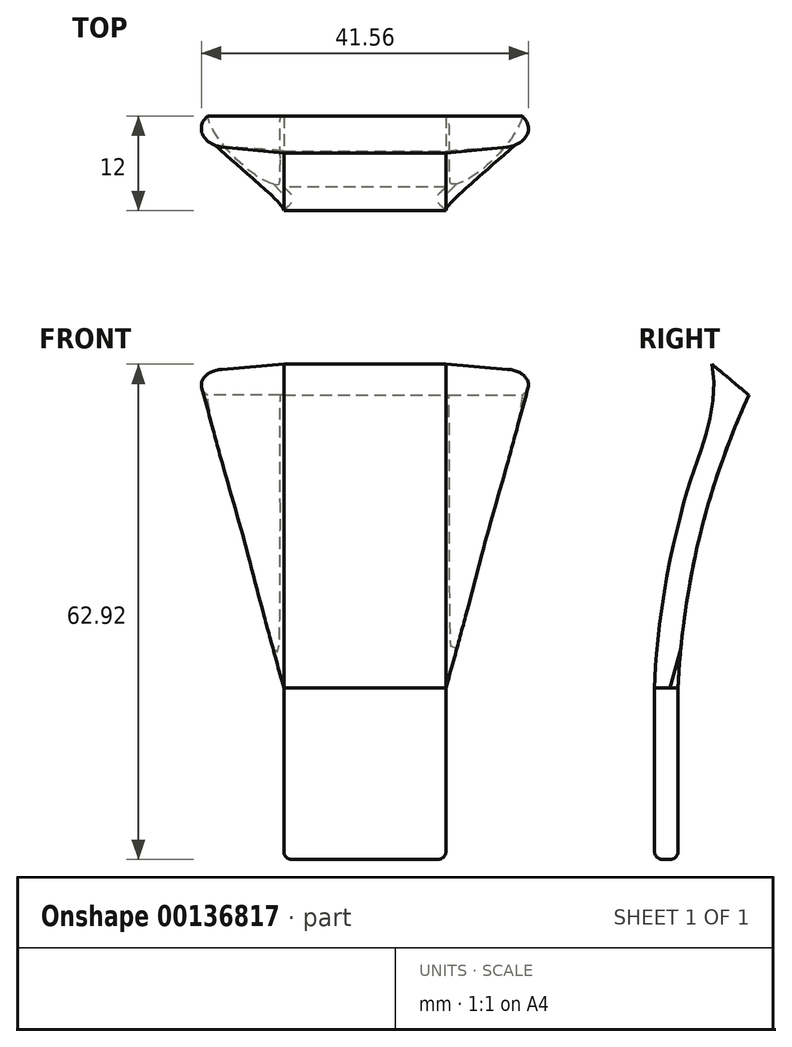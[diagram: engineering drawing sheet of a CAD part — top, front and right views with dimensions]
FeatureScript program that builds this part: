
annotation { "Feature Type Name" : "Feature", "Feature Type Description" : "" }
export const myFeature = defineFeature(function(context is Context, id is Id, definition is map)
    precondition{}
    {
        {
            var Q0;
            Q0=qCreatedBy(makeId("Front.planeOp"),FACE);
            var sketch = newSketch(context, id + "F0", { "sketchPlane" : qUnion([Q0])});
            skLineSegment(sketch, "E0.bottom", {"start": v(0, 0) * mm, "end": v(-20.6, 0) * mm});
            skLineSegment(sketch, "E0.top", {"start": v(0, 21.8) * mm, "end": v(-20.6, 21.8) * mm});
            skLineSegment(sketch, "E0.left", {"start": v(0, 0) * mm, "end": v(0, 21.8) * mm});
            skLineSegment(sketch, "E0.right", {"start": v(-20.6, 0) * mm, "end": v(-20.6, 21.8) * mm});
            skLineSegment(sketch, "E1", {"start": v(-10.3, 21.8) * mm, "end": v(-10.3, 0) * mm, "construction": true});
            skSolve(sketch);
        }
        {
            var Q0;
            Q0 = qSketchRegion(id + "F0", true);
            var Q1;
            Q1=makeQuery(id+"F0.imprint","IMPRINT",FACE,{"disambiguationData":[TD([[makeQuery(id+"F0.imprint","IMPRINT",EDGE,{"derivedFrom":sQuery(id+"F0.wireOp",EDGE,"E0.bottom")}),-1.0]])]});
            extrude(context, id + "F1", {"entities" : qUnion([Q0, Q1]), "depth" : 3 * mm});
        }
        {
            var Q0;
            Q0=qCreatedBy(makeId("Right.planeOp"),FACE);
            var sketch = newSketch(context, id + "F2", { "sketchPlane" : qUnion([Q0])});
            skArc(sketch, "E2", {"start": v(9, 58.98) * mm, "mid": v(2.7, 40.83) * mm, "end": v(0, 21.8) * mm});
            skLineSegment(sketch, "E3", {"start": v(9, 58.98) * mm, "end": v(9, 21.8) * mm, "construction": true});
            skLineSegment(sketch, "E4", {"start": v(0, 21.8) * mm, "end": v(-3, 21.8) * mm});
            skLineSegment(sketch, "E5", {"start": v(0, 21.8) * mm, "end": v(9, 21.8) * mm, "construction": true});
            skLineSegment(sketch, "E6", {"start": v(9, 58.98) * mm, "end": v(6.6, 61) * mm});
            skLineSegment(sketch, "E7", {"start": v(9, 58.98) * mm, "end": v(-3.17, 58.98) * mm, "construction": true});
            skLineSegment(sketch, "E8", {"start": v(6.6, 61) * mm, "end": v(4.3, 62.92) * mm});
            skFitSpline(sketch, "E9", {"points": [v(-3, 21.8) * mm, v(-2.7, 26.37) * mm, v(-1.58, 35) * mm, v(0.14, 43) * mm, v(1.64, 48.28) * mm, v(3.1, 52.6) * mm, v(4.3, 62.92) * mm], "startDerivative": vector(1.53, 30.61) * mm, "endDerivative": vector(-11.43, 51.05) * mm});
            skSolve(sketch);
        }
        {
            var Q0;
            Q0 = qSketchRegion(id + "F2", true);
            var Q1;
            Q1=makeQuery(id+"F2.imprint","IMPRINT",FACE,{"disambiguationData":[TD([[makeQuery(id+"F2.imprint","IMPRINT",EDGE,{"derivedFrom":sQuery(id+"F2.wireOp",EDGE,"E2")}),-1.0]])]});
            extrude(context, id + "F3", {"entities" : qUnion([Q0, Q1]), "oppositeDirection" : true, "depth" : 20.6 * mm});
        }
        {
            var Q0;
            Q0=makeQuery(id+"F1.opExtrude","SWEPT_EDGE",EDGE,{"disambiguationData":[OSD([sQuery(id+"F0.wireOp",EDGE,"E0.bottom"),sQuery(id+"F0.wireOp",EDGE,"E0.left")])]});
            var Q1;
            Q1=makeQuery(id+"F1.opExtrude","CAP_EDGE",EDGE,{"disambiguationData":[OSD([sQuery(id+"F0.wireOp",EDGE,"E0.bottom")])],"isStart":false});
            var Q2;
            Q2=makeQuery(id+"F1.opExtrude","SWEPT_EDGE",EDGE,{"disambiguationData":[OSD([sQuery(id+"F0.wireOp",EDGE,"E0.bottom"),sQuery(id+"F0.wireOp",EDGE,"E0.right")])]});
            var Q3;
            Q3=makeQuery(id+"F1.opExtrude","CAP_EDGE",EDGE,{"disambiguationData":[OSD([sQuery(id+"F0.wireOp",EDGE,"E0.bottom")])],"isStart":true});
            fillet(context, id + "F4", {"entities" : qUnion([Q0, Q1, Q2, Q3]), "radius" : 1 * mm, "tangentPropagation" : true, "allowEdgeOverflow" : false});
        }
        {
            var Q0;
            Q0=makeQuery(id+"F3.opExtrude","SWEPT_FACE",FACE,{"disambiguationData":[OSD([sQuery(id+"F2.wireOp",EDGE,"E6"),sQuery(id+"F2.wireOp",EDGE,"E8")])]});
            var sketch = newSketch(context, id + "F5", { "sketchPlane" : qUnion([Q0])});
            skLineSegment(sketch, "E10", {"start": v(0, -31.02) * mm, "end": v(9.69, -31.02) * mm});
            skLineSegment(sketch, "E11", {"start": v(7.82, -36.12) * mm, "end": v(0, -37.16) * mm});
            skArc(sketch, "E12", {"start": v(7.82, -36.12) * mm, "mid": v(10.3, -34.13) * mm, "end": v(9.69, -31.02) * mm});
            skLineSegment(sketch, "E13", {"start": v(-10.3, -31.02) * mm, "end": v(-10.3, -37.16) * mm, "construction": true});
            skLineSegment(sketch, "E14.MirrorCS", {"start": v(-20.6, -31.02) * mm, "end": v(-30.29, -31.02) * mm});
            skLineSegment(sketch, "E15.MirrorCS", {"start": v(-28.42, -36.12) * mm, "end": v(-20.6, -37.16) * mm});
            skArc(sketch, "E16.MirrorCS", {"start": v(-28.42, -36.12) * mm, "mid": v(-30.9, -34.13) * mm, "end": v(-30.29, -31.02) * mm});
            skSolve(sketch);
        }
        {
            var Q0;
            Q0=makeQuery(id+"F1.opExtrude","SWEPT_FACE",FACE,{"disambiguationData":[OSD([sQuery(id+"F0.wireOp",EDGE,"E0.top")])]});
            var sketch = newSketch(context, id + "F6", { "sketchPlane" : qUnion([Q0])});
            skLineSegment(sketch, "E17.bottom", {"start": v(0, 0) * mm, "end": v(-0.5, 0) * mm});
            skLineSegment(sketch, "E17.top", {"start": v(0, -3) * mm, "end": v(-0.5, -3) * mm});
            skLineSegment(sketch, "E17.left", {"start": v(0, 0) * mm, "end": v(0, -3) * mm});
            skLineSegment(sketch, "E17.right", {"start": v(-0.5, 0) * mm, "end": v(-0.5, -3) * mm});
            skLineSegment(sketch, "E18.bottom", {"start": v(-20.6, 0) * mm, "end": v(-20.1, 0) * mm});
            skLineSegment(sketch, "E18.top", {"start": v(-20.6, -3) * mm, "end": v(-20.1, -3) * mm});
            skLineSegment(sketch, "E18.left", {"start": v(-20.6, 0) * mm, "end": v(-20.6, -3) * mm});
            skLineSegment(sketch, "E18.right", {"start": v(-20.1, 0) * mm, "end": v(-20.1, -3) * mm});
            skSolve(sketch);
        }
        {
            var Q0;
            Q0=makeQuery(id+"F5.imprint","IMPRINT",FACE,{"disambiguationData":[TD([[makeQuery(id+"F5.imprint","IMPRINT",EDGE,{"derivedFrom":sQuery(id+"F5.wireOp",EDGE,"E10")}),-1.0]])]});
            var Q1;
            Q1=makeQuery(id+"F6.imprint","IMPRINT",FACE,{"disambiguationData":[TD([[makeQuery(id+"F6.imprint","IMPRINT",EDGE,{"derivedFrom":sQuery(id+"F6.wireOp",EDGE,"E17.bottom")}),1.0]])]});
            var Q2;
            Q2=sQuery(id+"F2.wireOp",EDGE,"E9");
            var Q3;
            Q3=sQuery(id+"F2.wireOp",EDGE,"E2");
            loft(context, id + "F7", {"addGuides" : true, "sheetProfilesArray" : [{ "sheetProfileEntities" : qUnion([Q0]) }, { "sheetProfileEntities" : qUnion([Q1]) }], "guidesArray" : [{ "guideEntities" : qUnion([Q2]), "guideDerivativeType" : LoftGuideDerivativeType.DEFAULT, "guideDerivativeMagnitude" : 1 }, { "guideEntities" : qUnion([Q3]), "guideDerivativeType" : LoftGuideDerivativeType.DEFAULT, "guideDerivativeMagnitude" : 1 }]});
        }
        {
            var Q1;
            Q1=makeQuery(id+"F5.imprint","IMPRINT",FACE,{"disambiguationData":[TD([[makeQuery(id+"F5.imprint","IMPRINT",EDGE,{"derivedFrom":sQuery(id+"F5.wireOp",EDGE,"E14.MirrorCS")}),1.0]])]});
            var Q2;
            Q2=makeQuery(id+"F6.imprint","IMPRINT",FACE,{"disambiguationData":[TD([[makeQuery(id+"F6.imprint","IMPRINT",EDGE,{"derivedFrom":sQuery(id+"F6.wireOp",EDGE,"E18.bottom")}),1.0]])]});
            var Q3;
            Q3=makeQuery(id+"F3.opExtrude","CAP_EDGE",EDGE,{"disambiguationData":[OSD([sQuery(id+"F2.wireOp",EDGE,"E2")])],"isStart":false});
            var Q4;
            Q4=makeQuery(id+"F3.opExtrude","CAP_EDGE",EDGE,{"disambiguationData":[OSD([sQuery(id+"F2.wireOp",EDGE,"E9")])],"isStart":false});
            var Q5;
            Q5=sQuery(id+"F5.wireOp",VERTEX,"E16.MirrorCS.start");
            var Q6;
            Q6=sQuery(id+"F6.wireOp",VERTEX,"E18.left.end");
            loft(context, id + "F8", {"operationType" : NewBodyOperationType.ADD, "addGuides" : true, "sheetProfilesArray" : [{ "sheetProfileEntities" : qUnion([Q1]) }, { "sheetProfileEntities" : qUnion([Q2]) }], "guidesArray" : [{ "guideEntities" : qUnion([Q3]), "guideDerivativeType" : LoftGuideDerivativeType.DEFAULT, "guideDerivativeMagnitude" : 1 }, { "guideEntities" : qUnion([Q4]), "guideDerivativeType" : LoftGuideDerivativeType.DEFAULT, "guideDerivativeMagnitude" : 1 }], "connections" : [{ "connectionEntities" : qUnion([Q5, Q6]), "connectionEdgeQueries" : qUnion([]), "connectionEdgeParameters" : [] }]});
        }
        {
            var Q0;
            Q0=makeQuery(id+"F0.imprint","IMPRINT",FACE,{"disambiguationData":[TD([[makeQuery(id+"F0.imprint","IMPRINT",EDGE,{"derivedFrom":sQuery(id+"F0.wireOp",EDGE,"E0.bottom")}),-1.0]])]});
            extrude(context, id + "F9", {"entities" : qUnion([Q0]), "depth" : 3 * mm});
        }
        {
            var Q0;
            Q0 = qSketchRegion(id + "F2", true);
            extrude(context, id + "F10", {"entities" : qUnion([Q0]), "operationType" : NewBodyOperationType.INTERSECT, "endBound" : BoundingType.SYMMETRIC, "oppositeDirection" : true, "depth" : 100 * mm, "hasSecondDirection" : true, "secondDirectionOppositeDirection" : false, "secondDirectionDepth" : 25 * mm});
        }
        {
            var Q0;
            Q0 = qSketchRegion(id + "F0", true);
            var Q1;
            Q1=makeQuery(id+"F0.imprint","IMPRINT",FACE,{"disambiguationData":[TD([[makeQuery(id+"F0.imprint","IMPRINT",EDGE,{"derivedFrom":sQuery(id+"F0.wireOp",EDGE,"E0.bottom")}),-1.0]])]});
            extrude(context, id + "F11", {"entities" : qUnion([Q0, Q1]), "operationType" : NewBodyOperationType.ADD, "depth" : 3 * mm});
        }
        {
            var Q0;
            Q0=makeQuery(id+"F11.opExtrude","SWEPT_FACE",FACE,{"disambiguationData":[OSD([sQuery(id+"F0.wireOp",EDGE,"E0.bottom")])]});
            fillet(context, id + "F12", {"entities" : qUnion([Q0]), "radius" : 1 * mm, "tangentPropagation" : true, "allowEdgeOverflow" : false});
        }
        {
            var Q0;
            Q0=makeQuery(id+"F1.opExtrude","SWEPT_BODY",BODY,{"disambiguationData":[OSD([sQuery(id+"F0.wireOp",EDGE,"E0.bottom"),sQuery(id+"F0.wireOp",EDGE,"E0.top"),sQuery(id+"F0.wireOp",EDGE,"E0.left"),sQuery(id+"F0.wireOp",EDGE,"E0.right")])]});
            transform(context, id + "F13", {"entities" : qUnion([Q0]), "transformType" : TransformType.TRANSLATION_3D, "dx" : 0 * mm, "dy" : 0 * mm, "dz" : 0 * mm, "makeCopy" : true});
        }
        {
            var Q0;
            Q0=makeQuery(id+"F13.opPattern","COPY",BODY,{"derivedFrom":makeQuery(id+"F1.opExtrude","SWEPT_BODY",BODY,{"disambiguationData":[OSD([sQuery(id+"F0.wireOp",EDGE,"E0.bottom"),sQuery(id+"F0.wireOp",EDGE,"E0.top"),sQuery(id+"F0.wireOp",EDGE,"E0.left"),sQuery(id+"F0.wireOp",EDGE,"E0.right")])]}),"instanceName":"1"});
            deleteBodies(context, id + "F14", {"entities" : qUnion([Q0])});
        }
    });
